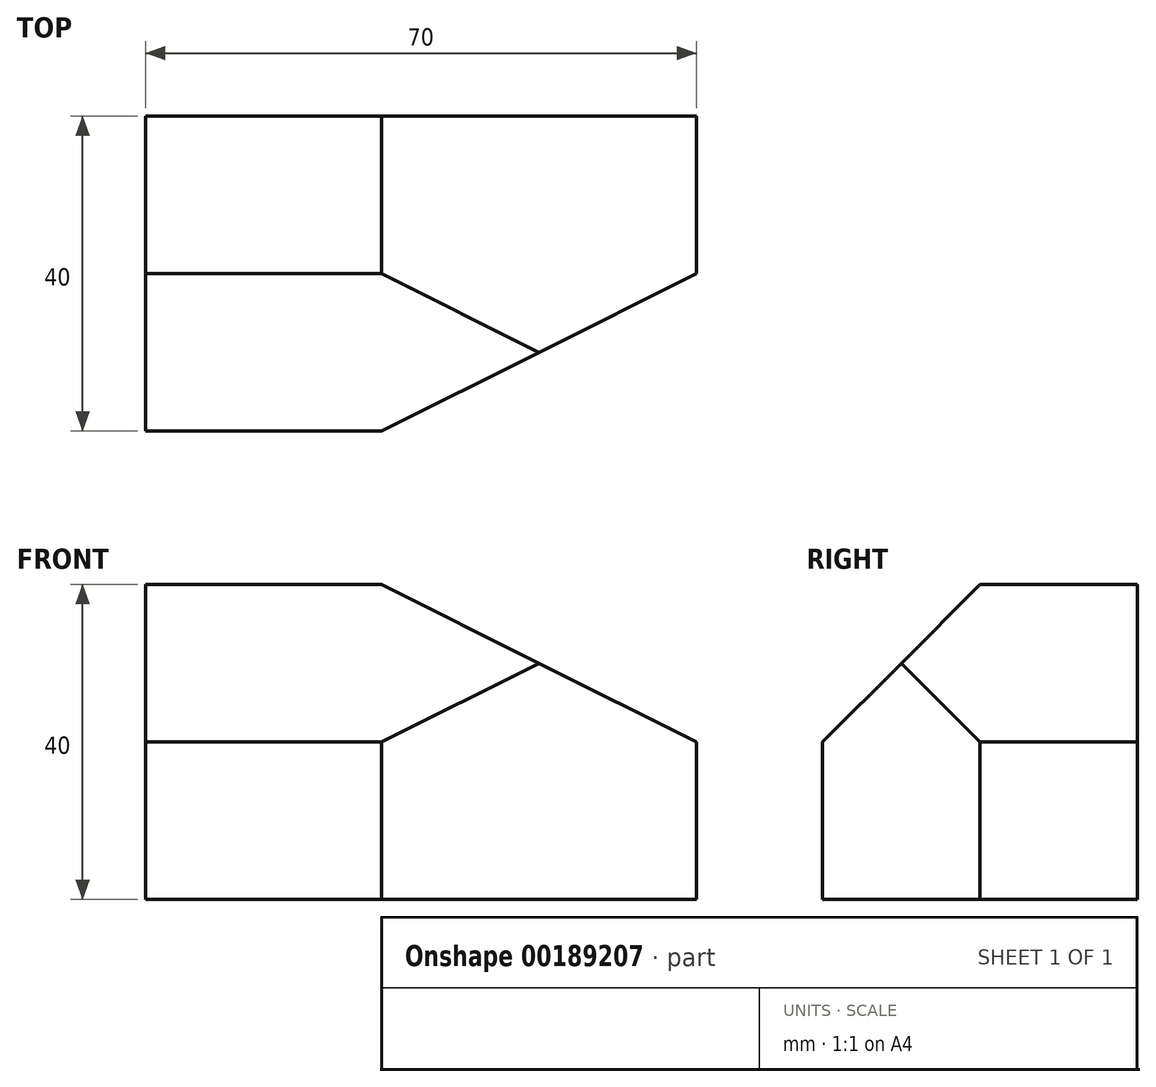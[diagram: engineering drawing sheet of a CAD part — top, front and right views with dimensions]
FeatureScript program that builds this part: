
annotation { "Feature Type Name" : "Feature", "Feature Type Description" : "" }
export const myFeature = defineFeature(function(context is Context, id is Id, definition is map)
    precondition{}
    {
        {
            var Q0;
            Q0=qCreatedBy(makeId("Top.planeOp"),FACE);
            var sketch = newSketch(context, id + "F0", { "sketchPlane" : qUnion([Q0])});
            skLineSegment(sketch, "E0.bottom", {"start": v(0, 0) * mm, "end": v(70, 0) * mm});
            skLineSegment(sketch, "E0.top", {"start": v(0, 40) * mm, "end": v(70, 40) * mm});
            skLineSegment(sketch, "E0.left", {"start": v(0, 0) * mm, "end": v(0, 40) * mm});
            skLineSegment(sketch, "E0.right", {"start": v(70, 0) * mm, "end": v(70, 40) * mm});
            skSolve(sketch);
        }
        {
            var Q0;
            Q0=makeQuery(id+"F0.imprint","IMPRINT",FACE,{"disambiguationData":[TD([[makeQuery(id+"F0.imprint","IMPRINT",EDGE,{"derivedFrom":sQuery(id+"F0.wireOp",EDGE,"E0.bottom")}),1.0]])]});
            extrude(context, id + "F1", {"entities" : qUnion([Q0]), "depth" : 40 * mm});
        }
        {
            var Q0;
            Q0=makeQuery(id+"F1.opExtrude","CAP_EDGE",EDGE,{"disambiguationData":[OSD([sQuery(id+"F0.wireOp",EDGE,"E0.bottom")])],"isStart":false});
            chamfer(context, id + "F2", {"entities" : qUnion([Q0]), "width" : 20 * mm, "tangentPropagation" : true});
        }
        {
            var Q0;
            Q0=makeQuery(id+"F1.opExtrude","CAP_EDGE",EDGE,{"disambiguationData":[OSD([sQuery(id+"F0.wireOp",EDGE,"E0.right")])],"isStart":false});
            chamfer(context, id + "F3", {"entities" : qUnion([Q0]), "chamferType" : ChamferType.TWO_OFFSETS, "width1" : 40 * mm, "oppositeDirection" : false, "width2" : 20 * mm, "tangentPropagation" : true});
        }
        {
            var Q0;
            Q0=makeQuery(id+"F1.opExtrude","SWEPT_EDGE",EDGE,{"disambiguationData":[OSD([sQuery(id+"F0.wireOp",EDGE,"E0.bottom"),sQuery(id+"F0.wireOp",EDGE,"E0.right")])]});
            chamfer(context, id + "F4", {"entities" : qUnion([Q0]), "chamferType" : ChamferType.TWO_OFFSETS, "width1" : 40 * mm, "oppositeDirection" : true, "width2" : 20 * mm, "tangentPropagation" : true});
        }
        {
            var Q0;
            {var subQ0=sQuery(id+"F0.wireOp",EDGE,"E0.right");var subQ1=sQuery(id+"F0.wireOp",EDGE,"E0.bottom");Q0=makeQuery(id+"F3.opChamfer","BLEND_VERTEX",VERTEX,{"blendedFrom":[makeQuery(id+"F1.opExtrude","CAP_EDGE",EDGE,{"disambiguationData":[OSD([subQ0])],"isStart":false}),makeQuery(id+"F2.opChamfer","BLEND_FACE",FACE,{"disambiguationData":[OSD([subQ1])]}),makeQuery(id+"F1.opExtrude","CAP_FACE",FACE,{"disambiguationData":[OSD([subQ1,sQuery(id+"F0.wireOp",EDGE,"E0.top"),sQuery(id+"F0.wireOp",EDGE,"E0.left"),subQ0])],"isStart":false})],"blendedInto":[makeQuery(id+"F2.opChamfer","BLEND_FACE",FACE,{"disambiguationData":[OSD([subQ1])]}),makeQuery(id+"F1.opExtrude","CAP_FACE",FACE,{"disambiguationData":[OSD([subQ1,sQuery(id+"F0.wireOp",EDGE,"E0.top"),sQuery(id+"F0.wireOp",EDGE,"E0.left"),subQ0])],"isStart":false})]});}
            var Q1;
            {var subQ0=sQuery(id+"F0.wireOp",EDGE,"E0.bottom");Q1=makeQuery(id+"F4.opChamfer","BLEND_VERTEX",VERTEX,{"blendedFrom":[makeQuery(id+"F1.opExtrude","SWEPT_EDGE",EDGE,{"disambiguationData":[OSD([subQ0,sQuery(id+"F0.wireOp",EDGE,"E0.right")])]}),makeQuery(id+"F1.opExtrude","SWEPT_FACE",FACE,{"disambiguationData":[OSD([subQ0])]}),makeQuery(id+"F2.opChamfer","BLEND_FACE",FACE,{"disambiguationData":[OSD([subQ0])]})],"blendedInto":[makeQuery(id+"F1.opExtrude","SWEPT_FACE",FACE,{"disambiguationData":[OSD([subQ0])]}),makeQuery(id+"F2.opChamfer","BLEND_FACE",FACE,{"disambiguationData":[OSD([subQ0])]})]});}
            var Q2;
            {var subQ0=sQuery(id+"F0.wireOp",EDGE,"E0.right");Q2=makeQuery(id+"F4.opChamfer","BLEND_VERTEX",VERTEX,{"blendedFrom":[makeQuery(id+"F1.opExtrude","SWEPT_EDGE",EDGE,{"disambiguationData":[OSD([sQuery(id+"F0.wireOp",EDGE,"E0.bottom"),subQ0])]}),makeQuery(id+"F3.opChamfer","BLEND_FACE",FACE,{"disambiguationData":[OSD([subQ0])]}),makeQuery(id+"F1.opExtrude","SWEPT_FACE",FACE,{"disambiguationData":[OSD([subQ0])]})],"blendedInto":[makeQuery(id+"F3.opChamfer","BLEND_FACE",FACE,{"disambiguationData":[OSD([subQ0])]}),makeQuery(id+"F1.opExtrude","SWEPT_FACE",FACE,{"disambiguationData":[OSD([subQ0])]})]});}
            cPlane(context, id + "F5", {"entities" : qUnion([Q0, Q1, Q2]), "cplaneType" : CPlaneType.THREE_POINT, "offset" : 25 * mm, "width" : 150 * mm, "height" : 150 * mm});
        }
        {
            var Q0;
            Q0=qCreatedBy(id+"F5.planeOp",FACE);
            var sketch = newSketch(context, id + "F6", { "sketchPlane" : qUnion([Q0])});
            skLineSegment(sketch, "E1", {"start": v(23.57, -42.43) * mm, "end": v(66, -28.28) * mm});
            skLineSegment(sketch, "E2", {"start": v(66, -28.28) * mm, "end": v(23.57, -14.14) * mm});
            skLineSegment(sketch, "E3", {"start": v(23.57, -14.14) * mm, "end": v(23.57, -42.43) * mm});
            skSolve(sketch);
        }
        {
            var Q0;
            Q0 = qSketchRegion(id + "F6", true);
            extrude(context, id + "F7", {"entities" : qUnion([Q0]), "operationType" : NewBodyOperationType.REMOVE, "endBound" : BoundingType.THROUGH_ALL, "oppositeDirection" : true, "depth" : 25 * mm});
        }
    });
